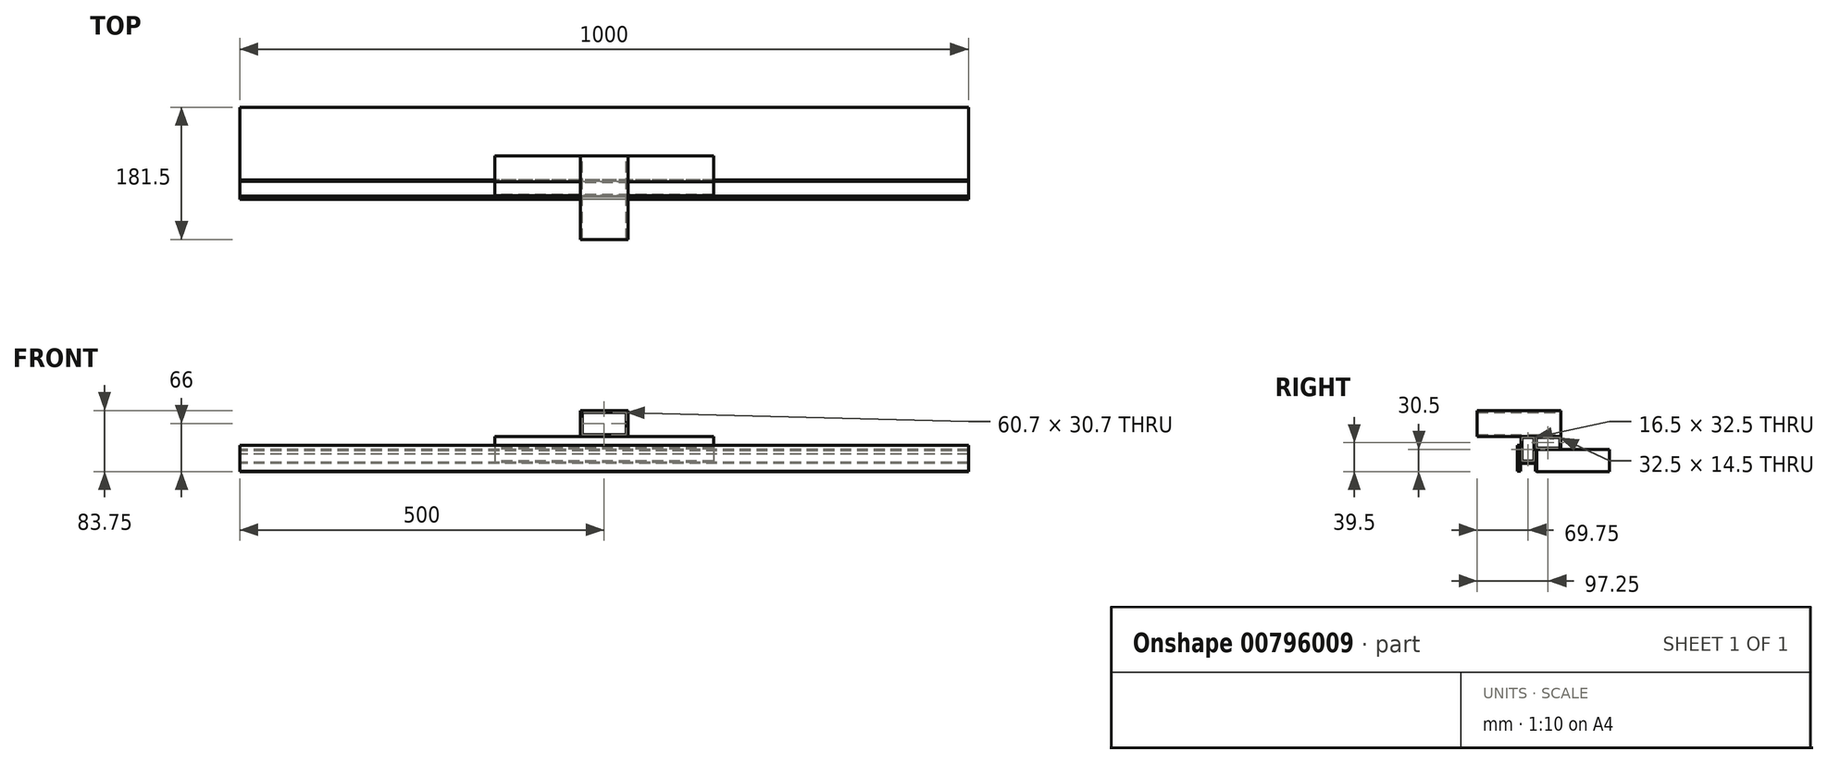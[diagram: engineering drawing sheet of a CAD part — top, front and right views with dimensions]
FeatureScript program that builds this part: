
annotation { "Feature Type Name" : "Feature", "Feature Type Description" : "" }
export const myFeature = defineFeature(function(context is Context, id is Id, definition is map)
    precondition{}
    {
        {
            var Q0;
            Q0=qCreatedBy(makeId("Right.planeOp"),FACE);
            var sketch = newSketch(context, id + "F0", { "sketchPlane" : qUnion([Q0])});
            skLineSegment(sketch, "E0", {"start": v(1.5, -34.9) * mm, "end": v(1.5, 0) * mm, "construction": true});
            skLineSegment(sketch, "E1.bottom", {"start": v(101.5, 18) * mm, "end": v(1.5, 18) * mm});
            skLineSegment(sketch, "E1.top", {"start": v(101.5, -12) * mm, "end": v(1.5, -12) * mm});
            skLineSegment(sketch, "E1.left", {"start": v(101.5, 18) * mm, "end": v(101.5, -12) * mm});
            skLineSegment(sketch, "E1.right", {"start": v(1.5, 18) * mm, "end": v(1.5, -12) * mm});
            skSolve(sketch);
        }
        {
            var Q0;
            Q0=qCreatedBy(makeId("Right.planeOp"),FACE);
            var sketch = newSketch(context, id + "F1", { "sketchPlane" : qUnion([Q0])});
            skLineSegment(sketch, "E2.bottom", {"start": v(0, -11.75) * mm, "end": v(1.5, -11.75) * mm});
            skLineSegment(sketch, "E2.top", {"start": v(0, 11.75) * mm, "end": v(1.5, 11.75) * mm});
            skLineSegment(sketch, "E2.left", {"start": v(0, -11.75) * mm, "end": v(0, -0.75) * mm});
            skLineSegment(sketch, "E2.right", {"start": v(1.5, -11.75) * mm, "end": v(1.5, 11.75) * mm});
            skLineSegment(sketch, "E3.left", {"start": v(0, 0) * mm, "end": v(0, 0) * mm});
            skLineSegment(sketch, "E4", {"start": v(0, 0.75) * mm, "end": v(0, 11.75) * mm});
            skLineSegment(sketch, "E5.bottom", {"start": v(0, -0.75) * mm, "end": v(-20.5, -0.75) * mm});
            skLineSegment(sketch, "E5.top", {"start": v(0, 0.75) * mm, "end": v(-20.5, 0.75) * mm});
            skPoint(sketch, "E5.middle", {"position": v(-10.25, 0) * mm});
            skLineSegment(sketch, "E6", {"start": v(-10.25, -22.4) * mm, "end": v(-10.25, 22.4) * mm, "construction": true});
            skPoint(sketch, "E6.startSnap0", {"position": v(-10.25, -0.75) * mm});
            skLineSegment(sketch, "E7.MirrorCS", {"start": v(-20.5, 0) * mm, "end": v(-20.5, 0) * mm});
            skLineSegment(sketch, "E8.MirrorCS", {"start": v(-22, -11.75) * mm, "end": v(-22, 11.75) * mm});
            skLineSegment(sketch, "E9.MirrorCS", {"start": v(-20.5, -11.75) * mm, "end": v(-20.5, -0.75) * mm});
            skLineSegment(sketch, "E10.MirrorCS", {"start": v(-20.5, 0.75) * mm, "end": v(-20.5, 11.75) * mm});
            skLineSegment(sketch, "E11.MirrorCS", {"start": v(-20.5, 11.75) * mm, "end": v(-22, 11.75) * mm});
            skLineSegment(sketch, "E12.MirrorCS", {"start": v(-20.5, -11.75) * mm, "end": v(-22, -11.75) * mm});
            skPoint(sketch, "E13.orphan", {"position": v(-20.5, -0.75) * mm});
            skPoint(sketch, "E14.MirrorCS.end.orphan", {"position": v(-20.5, 0.75) * mm});
            skSolve(sketch);
        }
        {
            var Q0;
            Q0=makeQuery(id+"F1.imprint","IMPRINT",FACE,{"disambiguationData":[TD([[makeQuery(id+"F1.imprint","IMPRINT",EDGE,{"derivedFrom":sQuery(id+"F1.wireOp",EDGE,"E2.bottom")}),1.0]])]});
            extrude(context, id + "F2", {"entities" : qUnion([Q0]), "endBound" : BoundingType.SYMMETRIC, "depth" : 1000 * mm, "offsetDistance" : 25 * mm});
        }
        {
            var Q0;
            Q0=qCreatedBy(makeId("Right.planeOp"),FACE);
            var sketch = newSketch(context, id + "F3", { "sketchPlane" : qUnion([Q0])});
            skLineSegment(sketch, "E15.bottom", {"start": v(-20, 36.25) * mm, "end": v(-0.5, 36.25) * mm});
            skLineSegment(sketch, "E15.top", {"start": v(-20, 0.75) * mm, "end": v(-0.5, 0.75) * mm});
            skLineSegment(sketch, "E15.left", {"start": v(-20, 36.25) * mm, "end": v(-20, 0.75) * mm});
            skLineSegment(sketch, "E15.right", {"start": v(-0.5, 36.25) * mm, "end": v(-0.5, 0.75) * mm});
            skLineSegment(sketch, "E16", {"start": v(-0.5, -12.98) * mm, "end": v(-0.5, 31.23) * mm, "construction": true});
            skLineSegment(sketch, "E17.0", {"start": v(-18.5, 34.75) * mm, "end": v(-18.5, 2.25) * mm});
            skLineSegment(sketch, "E17.1", {"start": v(-18.5, 34.75) * mm, "end": v(-2, 34.75) * mm});
            skLineSegment(sketch, "E17.2", {"start": v(-2, 34.75) * mm, "end": v(-2, 2.25) * mm});
            skLineSegment(sketch, "E17.3", {"start": v(-18.5, 2.25) * mm, "end": v(-2, 2.25) * mm});
            skSolve(sketch);
        }
        {
            var Q0;
            Q0=makeQuery(id+"F3.imprint","IMPRINT",FACE,{"disambiguationData":[TD([[makeQuery(id+"F3.imprint","IMPRINT",EDGE,{"derivedFrom":sQuery(id+"F3.wireOp",EDGE,"E15.bottom")}),-1.0]])]});
            extrude(context, id + "F4", {"entities" : qUnion([Q0]), "endBound" : BoundingType.SYMMETRIC, "depth" : 300 * mm, "offsetDistance" : 25 * mm});
        }
        {
            var Q0;
            Q0=qCreatedBy(makeId("Right.planeOp"),FACE);
            var sketch = newSketch(context, id + "F5", { "sketchPlane" : qUnion([Q0])});
            skLineSegment(sketch, "E18.bottom", {"start": v(-25, -11.75) * mm, "end": v(-22, -11.75) * mm});
            skLineSegment(sketch, "E18.top", {"start": v(-25, 23.75) * mm, "end": v(-22, 23.75) * mm});
            skLineSegment(sketch, "E18.left", {"start": v(-25, -11.75) * mm, "end": v(-25, 23.75) * mm});
            skLineSegment(sketch, "E18.right", {"start": v(-22, -11.75) * mm, "end": v(-22, 23.75) * mm});
            skSolve(sketch);
        }
        {
            var Q0;
            Q0=makeQuery(id+"F5.imprint","IMPRINT",FACE,{"disambiguationData":[TD([[makeQuery(id+"F5.imprint","IMPRINT",EDGE,{"derivedFrom":sQuery(id+"F5.wireOp",EDGE,"E18.bottom")}),1.0]])]});
            extrude(context, id + "F6", {"entities" : qUnion([Q0]), "endBound" : BoundingType.SYMMETRIC, "depth" : 1000 * mm, "offsetDistance" : 25 * mm});
        }
        {
            var Q0;
            Q0=qCreatedBy(makeId("Right.planeOp"),FACE);
            var sketch = newSketch(context, id + "F7", { "sketchPlane" : qUnion([Q0])});
            skLineSegment(sketch, "E19.bottom", {"start": v(-22, 23.75) * mm, "end": v(-20.5, 23.75) * mm});
            skLineSegment(sketch, "E19.top", {"start": v(-22, 16.25) * mm, "end": v(-20.5, 16.25) * mm});
            skLineSegment(sketch, "E19.left", {"start": v(-22, 23.75) * mm, "end": v(-22, 16.25) * mm});
            skLineSegment(sketch, "E19.right", {"start": v(-20.5, 23.75) * mm, "end": v(-20.5, 16.25) * mm});
            skSolve(sketch);
        }
        {
            var Q0;
            Q0 = qSketchRegion(id + "F7", true);
            extrude(context, id + "F8", {"entities" : qUnion([Q0]), "endBound" : BoundingType.SYMMETRIC, "depth" : 1000 * mm, "offsetDistance" : 25 * mm});
        }
        {
            var Q0;
            Q0=qCreatedBy(makeId("Right.planeOp"),FACE);
            var sketch = newSketch(context, id + "F9", { "sketchPlane" : qUnion([Q0])});
            skLineSegment(sketch, "E20.bottom", {"start": v(-0.5, 36.25) * mm, "end": v(35, 36.25) * mm});
            skLineSegment(sketch, "E20.top", {"start": v(-0.5, 18.75) * mm, "end": v(35, 18.75) * mm});
            skLineSegment(sketch, "E20.left", {"start": v(-0.5, 36.25) * mm, "end": v(-0.5, 18.75) * mm});
            skLineSegment(sketch, "E20.right", {"start": v(35, 36.25) * mm, "end": v(35, 18.75) * mm});
            skLineSegment(sketch, "E21.0", {"start": v(1, 20.25) * mm, "end": v(33.5, 20.25) * mm});
            skLineSegment(sketch, "E21.1", {"start": v(1, 34.75) * mm, "end": v(1, 20.25) * mm});
            skLineSegment(sketch, "E21.2", {"start": v(1, 34.75) * mm, "end": v(33.5, 34.75) * mm});
            skLineSegment(sketch, "E21.3", {"start": v(33.5, 34.75) * mm, "end": v(33.5, 20.25) * mm});
            skSolve(sketch);
        }
        {
            var Q0;
            Q0 = qSketchRegion(id + "F9", true);
            extrude(context, id + "F10", {"entities" : qUnion([Q0]), "endBound" : BoundingType.SYMMETRIC, "depth" : 300 * mm, "offsetDistance" : 25 * mm});
        }
        {
            var Q0;
            Q0=qCreatedBy(makeId("Front.planeOp"),FACE);
            var sketch = newSketch(context, id + "F11", { "sketchPlane" : qUnion([Q0])});
            skLineSegment(sketch, "E22.bottom", {"start": v(32.75, 36.25) * mm, "end": v(-32.75, 36.25) * mm});
            skLineSegment(sketch, "E22.top", {"start": v(32.75, 71.75) * mm, "end": v(-32.75, 71.75) * mm});
            skLineSegment(sketch, "E22.left", {"start": v(32.75, 36.25) * mm, "end": v(32.75, 71.75) * mm});
            skLineSegment(sketch, "E22.right", {"start": v(-32.75, 36.25) * mm, "end": v(-32.75, 71.75) * mm});
            skPoint(sketch, "E22.middle", {"position": v(0, 54) * mm});
            skLineSegment(sketch, "E23.0", {"start": v(30.35, 38.65) * mm, "end": v(-30.35, 38.65) * mm});
            skLineSegment(sketch, "E23.1", {"start": v(30.35, 38.65) * mm, "end": v(30.35, 69.35) * mm});
            skLineSegment(sketch, "E23.2", {"start": v(30.35, 69.35) * mm, "end": v(-30.35, 69.35) * mm});
            skLineSegment(sketch, "E23.3", {"start": v(-30.35, 38.65) * mm, "end": v(-30.35, 69.35) * mm});
            skSolve(sketch);
        }
        {
            var Q0;
            Q0 = qSketchRegion(id + "F11", true);
            extrude(context, id + "F12", {"entities" : qUnion([Q0]), "depth" : 80 * mm, "offsetDistance" : 25 * mm, "hasSecondDirection" : true, "secondDirectionOppositeDirection" : true, "secondDirectionDepth" : 35 * mm});
        }
        {
            var Q0;
            Q0 = qSketchRegion(id + "F0", true);
            extrude(context, id + "F13", {"entities" : qUnion([Q0]), "endBound" : BoundingType.SYMMETRIC, "depth" : 1000 * mm, "offsetDistance" : 25 * mm});
        }
    });
